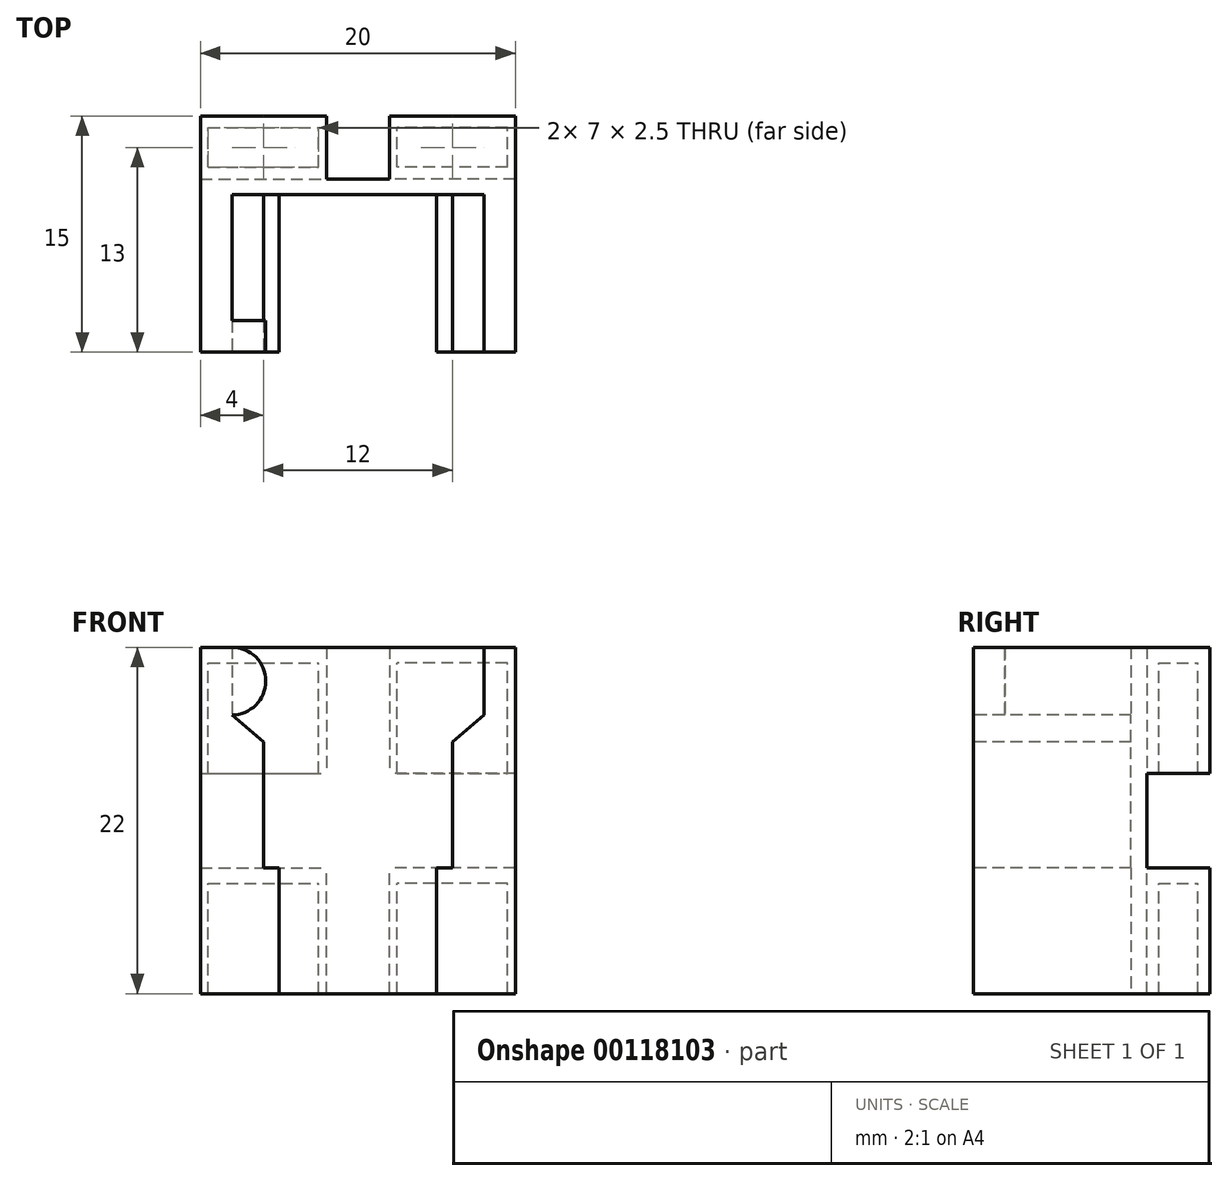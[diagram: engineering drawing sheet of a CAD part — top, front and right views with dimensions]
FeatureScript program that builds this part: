
annotation { "Feature Type Name" : "Feature", "Feature Type Description" : "" }
export const myFeature = defineFeature(function(context is Context, id is Id, definition is map)
    precondition{}
    {
        {
            var Q0;
            Q0=qCreatedBy(makeId("Front.planeOp"),FACE);
            var sketch = newSketch(context, id + "F0", { "sketchPlane" : qUnion([Q0])});
            skLineSegment(sketch, "E0.bottom", {"start": v(10, 11) * mm, "end": v(-10, 11) * mm});
            skLineSegment(sketch, "E0.top", {"start": v(10, -11) * mm, "end": v(-10, -11) * mm});
            skLineSegment(sketch, "E0.left", {"start": v(10, 11) * mm, "end": v(10, -11) * mm});
            skLineSegment(sketch, "E0.right", {"start": v(-10, 11) * mm, "end": v(-10, -11) * mm});
            skPoint(sketch, "E0.middle", {"position": v(0, 0) * mm});
            skSolve(sketch);
        }
        {
            var Q0;
            Q0=makeQuery(id+"F0.imprint","IMPRINT",FACE,{"disambiguationData":[TD([[makeQuery(id+"F0.imprint","IMPRINT",EDGE,{"derivedFrom":sQuery(id+"F0.wireOp",EDGE,"E0.bottom")}),1.0]])]});
            extrude(context, id + "F1", {"entities" : qUnion([Q0]), "depth" : 11 * mm});
        }
        {
            var Q0;
            Q0=makeQuery(id+"F1.opExtrude","CAP_FACE",FACE,{"disambiguationData":[OSD([sQuery(id+"F0.wireOp",EDGE,"E0.bottom"),sQuery(id+"F0.wireOp",EDGE,"E0.top"),sQuery(id+"F0.wireOp",EDGE,"E0.left"),sQuery(id+"F0.wireOp",EDGE,"E0.right")])],"isStart":false});
            var sketch = newSketch(context, id + "F2", { "sketchPlane" : qUnion([Q0])});
            skLineSegment(sketch, "E1.bottom", {"start": v(8, 11) * mm, "end": v(-8, 11) * mm});
            skLineSegment(sketch, "E1.left", {"start": v(8, 11) * mm, "end": v(8, 6.7) * mm});
            skLineSegment(sketch, "E1.right", {"start": v(-8, 11) * mm, "end": v(-8, 6.7) * mm});
            skPoint(sketch, "E1.middle", {"position": v(0, 0) * mm});
            skLineSegment(sketch, "E2.left", {"start": v(5, -3) * mm, "end": v(5, -11) * mm});
            skLineSegment(sketch, "E2.right", {"start": v(-5, -3) * mm, "end": v(-5, -11) * mm});
            skLineSegment(sketch, "E3", {"start": v(-5, -11) * mm, "end": v(5, -11) * mm});
            skLineSegment(sketch, "E4", {"start": v(5, -3) * mm, "end": v(6, -3) * mm});
            skLineSegment(sketch, "E5", {"start": v(6, -3) * mm, "end": v(6, 5) * mm});
            skLineSegment(sketch, "E6.MirrorCS", {"start": v(-5, -3) * mm, "end": v(-6, -3) * mm});
            skLineSegment(sketch, "E7.MirrorCS", {"start": v(-6, -3) * mm, "end": v(-6, 5) * mm});
            skLineSegment(sketch, "E8", {"start": v(-6, 5) * mm, "end": v(-8, 6.7) * mm});
            skLineSegment(sketch, "E9.MirrorCS", {"start": v(6, 5) * mm, "end": v(8, 6.7) * mm});
            skSolve(sketch);
        }
        {
            var Q0;
            Q0 = qSketchRegion(id + "F2", true);
            extrude(context, id + "F3", {"entities" : qUnion([Q0]), "operationType" : NewBodyOperationType.REMOVE, "oppositeDirection" : true, "depth" : 10 * mm});
        }
        {
            var Q0;
            {var subQ0=sQuery(id+"F0.wireOp",EDGE,"E0.right");var subQ1=sQuery(id+"F0.wireOp",EDGE,"E0.top");var subQ2=sQuery(id+"F0.wireOp",EDGE,"E0.bottom");Q0=makeQuery(id+"F3.boolean.opBoolean","SPLIT",FACE,{"disambiguationData":[TD([makeQuery(id+"F1.opExtrude","SWEPT_FACE",FACE,{"disambiguationData":[OSD([subQ0])]})])],"derivedFrom":makeQuery(id+"F1.opExtrude","CAP_FACE",FACE,{"disambiguationData":[OSD([subQ2,subQ1,sQuery(id+"F0.wireOp",EDGE,"E0.left"),subQ0])],"isStart":false})});}
            var sketch = newSketch(context, id + "F4", { "sketchPlane" : qUnion([Q0])});
            skArc(sketch, "E10", {"start": v(-8, 6.7) * mm, "mid": v(-5.85, 8.85) * mm, "end": v(-8, 11) * mm});
            skArc(sketch, "E11.MirrorCS", {"start": v(8, 6.7) * mm, "mid": v(5.85, 8.85) * mm, "end": v(8, 11) * mm});
            skLineSegment(sketch, "E12", {"start": v(-8, 11) * mm, "end": v(-8, 6.7) * mm});
            skLineSegment(sketch, "E13", {"start": v(8, 11) * mm, "end": v(8, 6.7) * mm});
            skSolve(sketch);
        }
        {
            var Q0;
            Q0=makeQuery(id+"F4.imprint","IMPRINT",FACE,{"disambiguationData":[TD([[makeQuery(id+"F4.imprint","IMPRINT",EDGE,{"derivedFrom":sQuery(id+"F4.wireOp",EDGE,"E10")}),1.0]])]});
            var Q1;
            Q1=makeQuery(id+"F4.imprint","IMPRINT",FACE,{"disambiguationData":[TD([[makeQuery(id+"F4.imprint","IMPRINT",EDGE,{"derivedFrom":sQuery(id+"F4.wireOp",EDGE,"E11.MirrorCS")}),-1.0]])]});
            extrude(context, id + "F5", {"entities" : qUnion([Q0, Q1]), "operationType" : NewBodyOperationType.ADD, "oppositeDirection" : true, "depth" : 2 * mm});
        }
        {
            var Q0;
            Q0=makeQuery(id+"F1.opExtrude","CAP_FACE",FACE,{"disambiguationData":[OSD([sQuery(id+"F0.wireOp",EDGE,"E0.bottom"),sQuery(id+"F0.wireOp",EDGE,"E0.top"),sQuery(id+"F0.wireOp",EDGE,"E0.left"),sQuery(id+"F0.wireOp",EDGE,"E0.right")])],"isStart":true});
            var sketch = newSketch(context, id + "F6", { "sketchPlane" : qUnion([Q0])});
            skLineSegment(sketch, "E14.bottom", {"start": v(-10, 11) * mm, "end": v(-2, 11) * mm});
            skLineSegment(sketch, "E14.top", {"start": v(-10, 3) * mm, "end": v(-2, 3) * mm});
            skLineSegment(sketch, "E14.left", {"start": v(-10, 11) * mm, "end": v(-10, 3) * mm});
            skLineSegment(sketch, "E14.right", {"start": v(-2, 11) * mm, "end": v(-2, 3) * mm});
            skLineSegment(sketch, "E15.MirrorCS", {"start": v(2, 11) * mm, "end": v(2, 3) * mm});
            skLineSegment(sketch, "E16.MirrorCS", {"start": v(10, 11) * mm, "end": v(2, 11) * mm});
            skLineSegment(sketch, "E17.MirrorCS", {"start": v(10, 11) * mm, "end": v(10, 3) * mm});
            skLineSegment(sketch, "E18.MirrorCS", {"start": v(10, 3) * mm, "end": v(2, 3) * mm});
            skLineSegment(sketch, "E19.MirrorCS", {"start": v(-10, -3) * mm, "end": v(-2, -3) * mm});
            skLineSegment(sketch, "E20.MirrorCS", {"start": v(-2, -11) * mm, "end": v(-2, -3) * mm});
            skLineSegment(sketch, "E21.MirrorCS", {"start": v(-10, -11) * mm, "end": v(-10, -3) * mm});
            skLineSegment(sketch, "E22.MirrorCS", {"start": v(-10, -11) * mm, "end": v(-2, -11) * mm});
            skLineSegment(sketch, "E23.MirrorCS", {"start": v(10, -11) * mm, "end": v(2, -11) * mm});
            skLineSegment(sketch, "E24.MirrorCS", {"start": v(2, -11) * mm, "end": v(2, -3) * mm});
            skLineSegment(sketch, "E25.MirrorCS", {"start": v(10, -3) * mm, "end": v(2, -3) * mm});
            skLineSegment(sketch, "E26.MirrorCS", {"start": v(10, -11) * mm, "end": v(10, -3) * mm});
            skSolve(sketch);
        }
        {
            var Q0;
            Q0 = qSketchRegion(id + "F6", true);
            extrude(context, id + "F7", {"entities" : qUnion([Q0]), "operationType" : NewBodyOperationType.ADD, "depth" : 4 * mm});
        }
        {
            var Q0;
            Q0=makeQuery(id+"F7.boolean.opBoolean","MERGE",FACE,{"derivedFrom":[makeQuery(id+"F1.opExtrude","SWEPT_FACE",FACE,{"disambiguationData":[OSD([sQuery(id+"F0.wireOp",EDGE,"E0.bottom")])]}),makeQuery(id+"F7.opExtrude","SWEPT_FACE",FACE,{"disambiguationData":[OSD([sQuery(id+"F6.wireOp",EDGE,"E14.bottom")])]}),makeQuery(id+"F7.opExtrude","SWEPT_FACE",FACE,{"disambiguationData":[OSD([sQuery(id+"F6.wireOp",EDGE,"E16.MirrorCS")])]})]});
            var sketch = newSketch(context, id + "F8", { "sketchPlane" : qUnion([Q0])});
            skLineSegment(sketch, "E27.bottom", {"start": v(-2.5, 3.25) * mm, "end": v(-9.5, 3.25) * mm});
            skLineSegment(sketch, "E27.top", {"start": v(-2.5, 0.75) * mm, "end": v(-9.5, 0.75) * mm});
            skLineSegment(sketch, "E27.left", {"start": v(-2.5, 3.25) * mm, "end": v(-2.5, 0.75) * mm});
            skLineSegment(sketch, "E27.right", {"start": v(-9.5, 3.25) * mm, "end": v(-9.5, 0.75) * mm});
            skPoint(sketch, "E27.middle", {"position": v(-6, 2) * mm});
            skLineSegment(sketch, "E28.MirrorCS", {"start": v(2.5, 3.25) * mm, "end": v(9.5, 3.25) * mm});
            skLineSegment(sketch, "E29.MirrorCS", {"start": v(9.5, 3.25) * mm, "end": v(9.5, 0.75) * mm});
            skLineSegment(sketch, "E30.MirrorCS", {"start": v(2.5, 0.75) * mm, "end": v(9.5, 0.75) * mm});
            skLineSegment(sketch, "E31.MirrorCS", {"start": v(2.5, 3.25) * mm, "end": v(2.5, 0.75) * mm});
            skSolve(sketch);
        }
        {
            var Q0;
            Q0=makeQuery(id+"F8.imprint","IMPRINT",FACE,{"disambiguationData":[TD([[makeQuery(id+"F8.imprint","IMPRINT",EDGE,{"derivedFrom":sQuery(id+"F8.wireOp",EDGE,"E27.bottom")}),1.0]])]});
            var Q1;
            Q1=makeQuery(id+"F8.imprint","IMPRINT",FACE,{"disambiguationData":[TD([[makeQuery(id+"F8.imprint","IMPRINT",EDGE,{"derivedFrom":sQuery(id+"F8.wireOp",EDGE,"E28.MirrorCS")}),-1.0]])]});
            extrude(context, id + "F9", {"entities" : qUnion([Q0, Q1]), "operationType" : NewBodyOperationType.REMOVE, "oppositeDirection" : true, "depth" : 25 * mm});
        }
        {
            var Q0;
            Q0=makeQuery(id+"F7.opExtrude","SWEPT_FACE",FACE,{"disambiguationData":[OSD([sQuery(id+"F6.wireOp",EDGE,"E19.MirrorCS")])]});
            var sketch = newSketch(context, id + "F10", { "sketchPlane" : qUnion([Q0])});
            skLineSegment(sketch, "E32.bottom", {"start": v(2, 4) * mm, "end": v(10, 4) * mm});
            skLineSegment(sketch, "E32.top", {"start": v(2, 0) * mm, "end": v(10, 0) * mm});
            skLineSegment(sketch, "E32.left", {"start": v(2, 4) * mm, "end": v(2, 0) * mm});
            skLineSegment(sketch, "E32.right", {"start": v(10, 4) * mm, "end": v(10, 0) * mm});
            skLineSegment(sketch, "E33.MirrorCS", {"start": v(-2, 4) * mm, "end": v(-2, 0) * mm});
            skLineSegment(sketch, "E34.MirrorCS", {"start": v(-2, 0) * mm, "end": v(-10, 0) * mm});
            skLineSegment(sketch, "E35.MirrorCS", {"start": v(-2, 4) * mm, "end": v(-10, 4) * mm});
            skLineSegment(sketch, "E36.MirrorCS", {"start": v(-10, 4) * mm, "end": v(-10, 0) * mm});
            skSolve(sketch);
        }
        {
            var Q0;
            Q0=makeQuery(id+"F7.boolean.opBoolean","MERGE",FACE,{"derivedFrom":[makeQuery(id+"F1.opExtrude","SWEPT_FACE",FACE,{"disambiguationData":[OSD([sQuery(id+"F0.wireOp",EDGE,"E0.bottom")])]}),makeQuery(id+"F7.opExtrude","SWEPT_FACE",FACE,{"disambiguationData":[OSD([sQuery(id+"F6.wireOp",EDGE,"E14.bottom")])]}),makeQuery(id+"F7.opExtrude","SWEPT_FACE",FACE,{"disambiguationData":[OSD([sQuery(id+"F6.wireOp",EDGE,"E16.MirrorCS")])]})]});
            var sketch = newSketch(context, id + "F11", { "sketchPlane" : qUnion([Q0])});
            skLineSegment(sketch, "E37.bottom", {"start": v(2, 4) * mm, "end": v(10, 4) * mm});
            skLineSegment(sketch, "E37.top", {"start": v(2, 0) * mm, "end": v(10, 0) * mm});
            skLineSegment(sketch, "E37.left", {"start": v(2, 4) * mm, "end": v(2, 0) * mm});
            skLineSegment(sketch, "E37.right", {"start": v(10, 4) * mm, "end": v(10, 0) * mm});
            skLineSegment(sketch, "E38.MirrorCS", {"start": v(-2, 4) * mm, "end": v(-2, 0) * mm});
            skLineSegment(sketch, "E39.MirrorCS", {"start": v(-2, 0) * mm, "end": v(-10, 0) * mm});
            skLineSegment(sketch, "E40.MirrorCS", {"start": v(-2, 4) * mm, "end": v(-10, 4) * mm});
            skLineSegment(sketch, "E41.MirrorCS", {"start": v(-10, 4) * mm, "end": v(-10, 0) * mm});
            skSolve(sketch);
        }
        {
            var Q0;
            Q0 = qSketchRegion(id + "F11", true);
            extrude(context, id + "F12", {"entities" : qUnion([Q0]), "operationType" : NewBodyOperationType.ADD, "oppositeDirection" : true, "depth" : 1 * mm});
        }
        {
            var Q0;
            Q0 = qSketchRegion(id + "F10", true);
            extrude(context, id + "F13", {"entities" : qUnion([Q0]), "operationType" : NewBodyOperationType.ADD, "oppositeDirection" : true, "depth" : 1 * mm});
        }
    });
